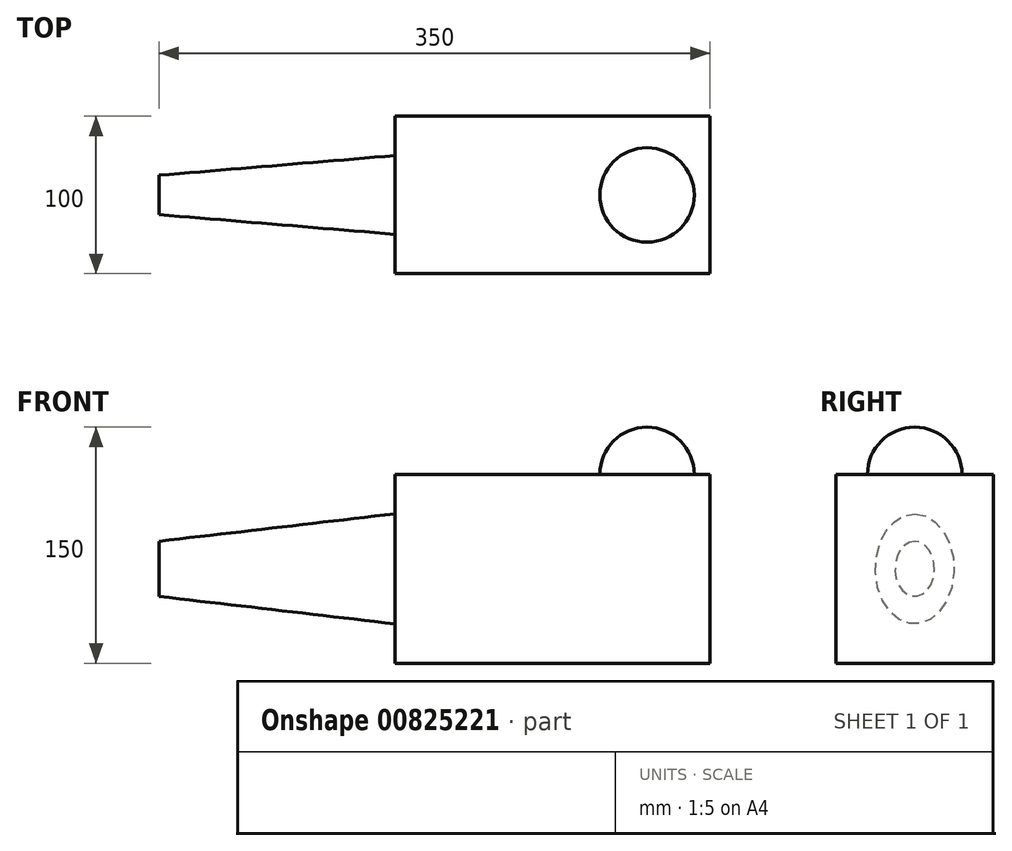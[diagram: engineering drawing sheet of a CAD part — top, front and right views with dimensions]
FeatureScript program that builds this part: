
annotation { "Feature Type Name" : "Feature", "Feature Type Description" : "" }
export const myFeature = defineFeature(function(context is Context, id is Id, definition is map)
    precondition{}
    {
        {
            var Q0;
            Q0=qCreatedBy(makeId("Top.planeOp"),FACE);
            var sketch = newSketch(context, id + "F0", { "sketchPlane" : qUnion([Q0])});
            skLineSegment(sketch, "E0.bottom", {"start": v(100, 50) * mm, "end": v(-100, 50) * mm});
            skLineSegment(sketch, "E0.top", {"start": v(100, -50) * mm, "end": v(-100, -50) * mm});
            skLineSegment(sketch, "E0.left", {"start": v(100, 50) * mm, "end": v(100, -50) * mm});
            skLineSegment(sketch, "E0.right", {"start": v(-100, 50) * mm, "end": v(-100, -50) * mm});
            skPoint(sketch, "E0.middle", {"position": v(0, 0) * mm});
            skSolve(sketch);
        }
        {
            var Q0;
            Q0 = qSketchRegion(id + "F0", true);
            extrude(context, id + "F1", {"entities" : qUnion([Q0]), "depth" : 120 * mm, "offsetDistance" : 25 * mm});
        }
        {
            var Q0;
            Q0=makeQuery(id+"F1.opExtrude","CAP_FACE",FACE,{"disambiguationData":[OSD([sQuery(id+"F0.wireOp",EDGE,"E0.bottom"),sQuery(id+"F0.wireOp",EDGE,"E0.top"),sQuery(id+"F0.wireOp",EDGE,"E0.left"),sQuery(id+"F0.wireOp",EDGE,"E0.right")])],"isStart":false});
            var sketch = newSketch(context, id + "F2", { "sketchPlane" : qUnion([Q0])});
            skArc(sketch, "E1", {"start": v(60, -30) * mm, "mid": v(90, 0) * mm, "end": v(60, 30) * mm});
            skLineSegment(sketch, "E2", {"start": v(60, 0) * mm, "end": v(60, 30) * mm});
            skLineSegment(sketch, "E3", {"start": v(60, 30) * mm, "end": v(60, -30) * mm});
            skPoint(sketch, "E4.orphan", {"position": v(-100, 0) * mm});
            skPoint(sketch, "E5.start.orphan", {"position": v(100, 0) * mm});
            skLineSegment(sketch, "E6", {"start": v(100, 0) * mm, "end": v(-100, 0) * mm, "construction": true});
            skSolve(sketch);
        }
        {
            var Q0;
            {var subQ0=sQuery(id+"F2.wireOp",EDGE,"E1");Q0=makeQuery(id+"F2.imprint","IMPRINT",FACE,{"disambiguationData":[TD([[makeQuery(id+"F2.imprint","IMPRINT",EDGE,{"derivedFrom":subQ0}),1.0]])]});}
            var Q1;
            Q1=sQuery(id+"F2.wireOp",EDGE,"E3");
            revolve(context, id + "F3", {"operationType" : NewBodyOperationType.ADD, "surfaceOperationType" : NewSurfaceOperationType.NEW, "entities" : qUnion([Q0]), "axis" : qUnion([Q1]), "revolveType" : RevolveType.ONE_DIRECTION, "angle" : 180 * degree});
        }
        {
            var Q0;
            Q0=makeQuery(id+"F1.opExtrude","SWEPT_FACE",FACE,{"disambiguationData":[OSD([sQuery(id+"F0.wireOp",EDGE,"E0.right")])]});
            var sketch = newSketch(context, id + "F4", { "sketchPlane" : qUnion([Q0])});
            skLineSegment(sketch, "E7", {"start": v(0, 0) * mm, "end": v(0, 120) * mm, "construction": true});
            skLineSegment(sketch, "E8", {"start": v(50, 60) * mm, "end": v(-50, 60) * mm, "construction": true});
            skEllipse(sketch, "E9", {"center": v(0, 60) * mm, "majorRadius": 35 * mm, "minorRadius": 25 * mm, "majorAxis": v(0, 1)});
            skSolve(sketch);
        }
        {
            var Q0;
            Q0=qCreatedBy(makeId("Right.planeOp"),FACE);
            cPlane(context, id + "F5", {"entities" : qUnion([Q0]), "cplaneType" : CPlaneType.OFFSET, "offset" : 250 * mm, "oppositeDirection" : true, "width" : 150 * mm, "height" : 150 * mm});
        }
        {
            var Q0;
            Q0=qCreatedBy(id+"F5.planeOp",FACE);
            var sketch = newSketch(context, id + "F6", { "sketchPlane" : qUnion([Q0])});
            skEllipse(sketch, "E10", {"center": v(0, 60) * mm, "majorRadius": 17.5 * mm, "minorRadius": 12.5 * mm, "majorAxis": v(0, 1)});
            skSolve(sketch);
        }
        {
            var Q1;
            Q1=makeQuery(id+"F4.imprint","IMPRINT",FACE,{"disambiguationData":[TD([[makeQuery(id+"F4.imprint","IMPRINT",EDGE,{"derivedFrom":sQuery(id+"F4.wireOp",EDGE,"E9")}),1.0]])]});
            var Q2;
            Q2=makeQuery(id+"F6.imprint","IMPRINT",FACE,{"disambiguationData":[TD([[makeQuery(id+"F6.imprint","IMPRINT",EDGE,{"derivedFrom":sQuery(id+"F6.wireOp",EDGE,"E10")}),1.0]])]});
            loft(context, id + "F7", {"operationType" : NewBodyOperationType.ADD, "sheetProfilesArray" : [{ "sheetProfileEntities" : qUnion([Q1]) }, { "sheetProfileEntities" : qUnion([Q2]) }]});
        }
    });
